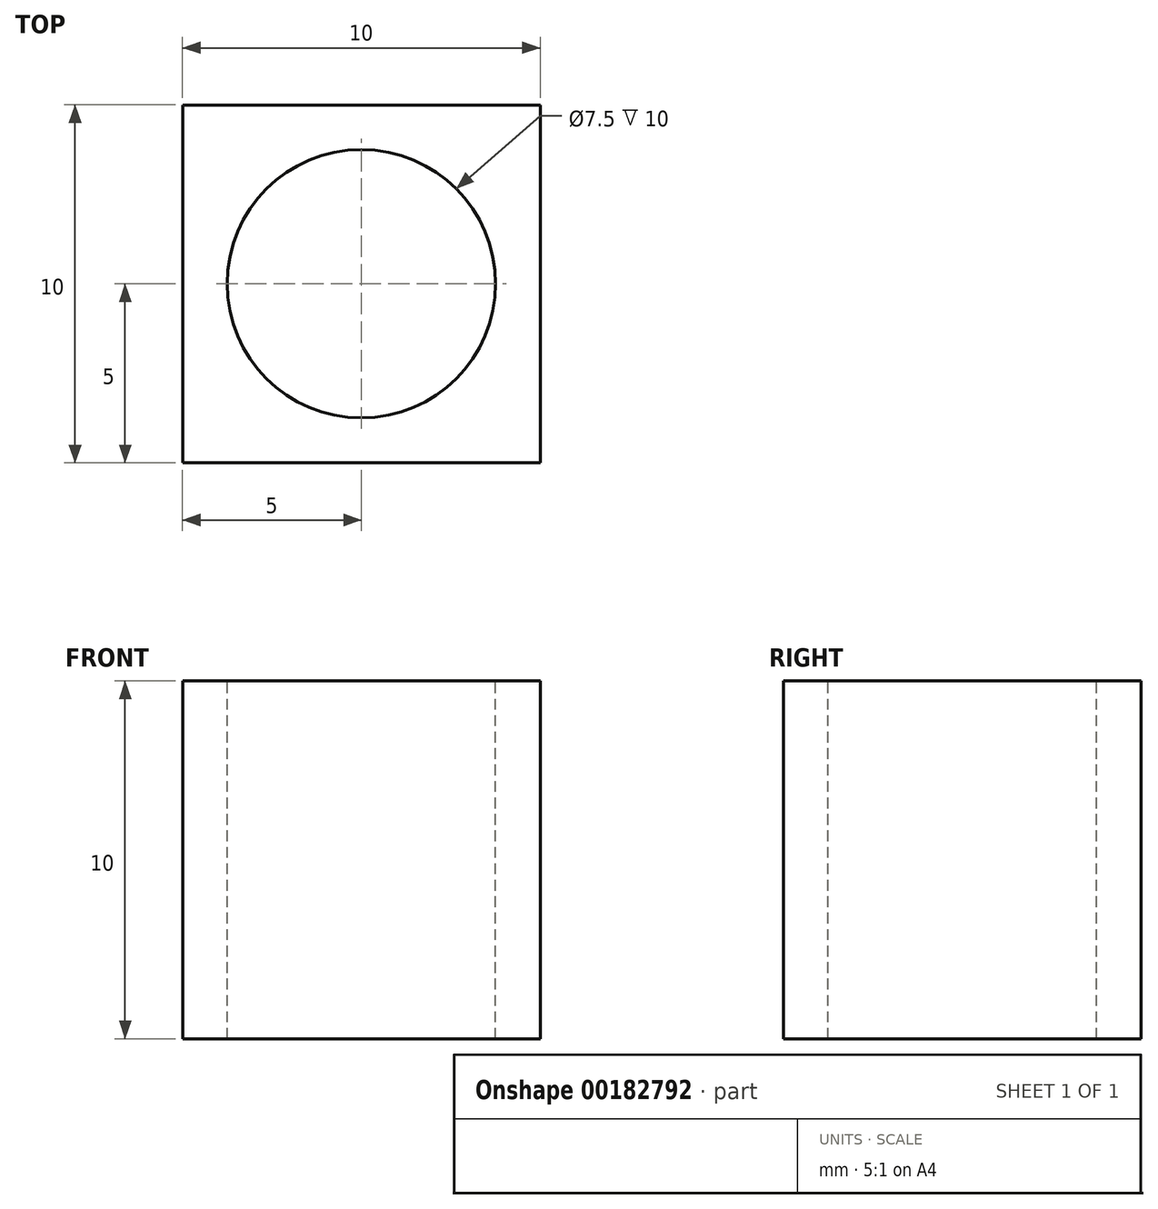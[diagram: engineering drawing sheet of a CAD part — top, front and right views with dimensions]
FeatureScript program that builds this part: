
annotation { "Feature Type Name" : "Feature", "Feature Type Description" : "" }
export const myFeature = defineFeature(function(context is Context, id is Id, definition is map)
    precondition{}
    {
        {
            var Q0;
            Q0=qCreatedBy(makeId("Top.planeOp"),FACE);
            var sketch = newSketch(context, id + "F0", { "sketchPlane" : qUnion([Q0])});
            skLineSegment(sketch, "E0.bottom", {"start": v(5, -5) * mm, "end": v(-5, -5) * mm});
            skLineSegment(sketch, "E0.top", {"start": v(5, 5) * mm, "end": v(-5, 5) * mm});
            skLineSegment(sketch, "E0.left", {"start": v(5, -5) * mm, "end": v(5, 5) * mm});
            skLineSegment(sketch, "E0.right", {"start": v(-5, -5) * mm, "end": v(-5, 5) * mm});
            skPoint(sketch, "E0.middle", {"position": v(0, 0) * mm});
            skSolve(sketch);
        }
        {
            var Q0;
            Q0=makeQuery(id+"F0.imprint","IMPRINT",FACE,{"disambiguationData":[TD([[makeQuery(id+"F0.imprint","IMPRINT",EDGE,{"derivedFrom":sQuery(id+"F0.wireOp",EDGE,"E0.bottom")}),-1.0]])]});
            extrude(context, id + "F1", {"entities" : qUnion([Q0]), "oppositeDirection" : true, "depth" : 10 * mm});
        }
        {
            var Q0;
            Q0=makeQuery(id+"F1.opExtrude","CAP_FACE",FACE,{"disambiguationData":[OSD([sQuery(id+"F0.wireOp",EDGE,"E0.bottom"),sQuery(id+"F0.wireOp",EDGE,"E0.top"),sQuery(id+"F0.wireOp",EDGE,"E0.left"),sQuery(id+"F0.wireOp",EDGE,"E0.right")])],"isStart":true});
            var sketch = newSketch(context, id + "F2", { "sketchPlane" : qUnion([Q0])});
            skPoint(sketch, "E1", {"position": v(0, 0) * mm});
            skSolve(sketch);
        }
        {
            var Q0;
            Q0=sQuery(id+"F2.wireOp",VERTEX,"E1");
            var Q1;
            Q1=makeQuery(id+"F1.opExtrude","SWEPT_BODY",BODY,{"disambiguationData":[OSD([sQuery(id+"F0.wireOp",EDGE,"E0.bottom"),sQuery(id+"F0.wireOp",EDGE,"E0.top"),sQuery(id+"F0.wireOp",EDGE,"E0.left"),sQuery(id+"F0.wireOp",EDGE,"E0.right")])]});
            hole(context, id + "F3", {"style" : HoleStyle.SIMPLE, "endStyle" : HoleEndStyle.THROUGH, "holeDiameter" : 7.5 * mm, "locations" : qUnion([Q0]), "scope" : qUnion([Q1]), "isTappedThrough" : true});
        }
    });
